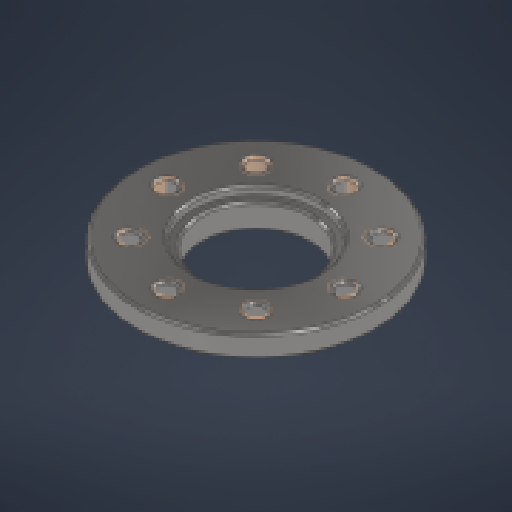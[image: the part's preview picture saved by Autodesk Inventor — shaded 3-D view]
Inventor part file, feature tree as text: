
AUTODESK INVENTOR PART (.ipt)
format: ipt  version: 2024 (Build 280153000, 153)  size: 268,800 bytes
history: native  units: mm
features: other x4, extrude x2, sketch x2, projected_geometry x2, chamfer x1
ambient origin geometry x8: Origin, YZ Plane, XZ Plane, XY Plane, X Axis, Y Axis, Z Axis, Center Point
bodies: Body1 (feature_tree), Body2 (feature_tree)
feature tree (11):
  other  "솔리드1"
  extrude  "돌출1"  Depth=16.5mm
  extrude  "돌출2"  Depth=80.0mm TaperAngle=360.0deg
  chamfer  "모따기1"  Distance=10.0mm
  sketch  "스케치1"
  projected_geometry  "투영된 루프1"
  sketch  "스케치2"
  projected_geometry  "투영된 루프2"
  other  "기준1"
  other  "복합1"
  other  "Srf1"
